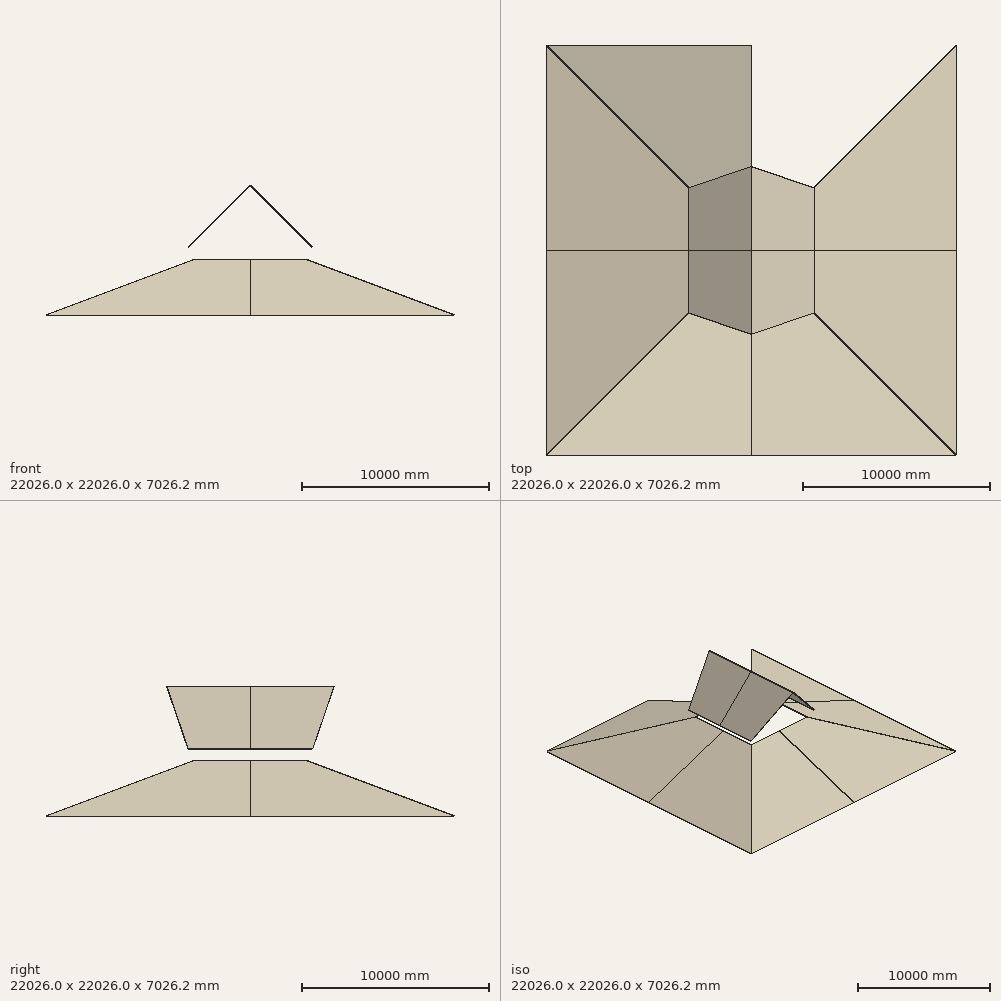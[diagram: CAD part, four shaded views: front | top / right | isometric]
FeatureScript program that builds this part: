
annotation { "Feature Type Name" : "Feature", "Feature Type Description" : "" }
export const myFeature = defineFeature(function(context is Context, id is Id, definition is map)
    precondition{}
    {
        {
            var Q0;
            Q0=qCreatedBy(makeId("Top.planeOp"),FACE);
            var sketch = newSketch(context, id + "F0", { "sketchPlane" : qUnion([Q0])});
            skLineSegment(sketch, "E0", {"start": v(0, 0) * mm, "end": v(0, -6000) * mm, "construction": true});
            skLineSegment(sketch, "E1", {"start": v(0, -6000) * mm, "end": v(6000, -6000) * mm, "construction": true});
            skLineSegment(sketch, "E2", {"start": v(6000, -6000) * mm, "end": v(6000, 0) * mm, "construction": true});
            skLineSegment(sketch, "E3", {"start": v(6000, 0) * mm, "end": v(10000, 0) * mm, "construction": true});
            skLineSegment(sketch, "E4", {"start": v(10000, 0) * mm, "end": v(10000, -10000) * mm, "construction": true});
            skLineSegment(sketch, "E5", {"start": v(10000, -10000) * mm, "end": v(-4000, -10000) * mm, "construction": true});
            skLineSegment(sketch, "E6", {"start": v(-4000, -10000) * mm, "end": v(-4000, 0) * mm, "construction": true});
            skLineSegment(sketch, "E7", {"start": v(-4000, 0) * mm, "end": v(0, 0) * mm, "construction": true});
            skLineSegment(sketch, "E8", {"start": v(3000, -6000) * mm, "end": v(3000, -8482.28) * mm, "construction": true});
            skLineSegment(sketch, "E9", {"start": v(0, -6000) * mm, "end": v(0, -10000) * mm, "construction": true});
            skLineSegment(sketch, "E10", {"start": v(-1000, 0) * mm, "end": v(-1000, -7000) * mm, "construction": true});
            skLineSegment(sketch, "E11", {"start": v(-1000, -7000) * mm, "end": v(7000, -7000) * mm, "construction": true});
            skLineSegment(sketch, "E12", {"start": v(7000, -7000) * mm, "end": v(7000, 0) * mm, "construction": true});
            skLineSegment(sketch, "E13", {"start": v(0, -6000) * mm, "end": v(-8000, -14000) * mm, "construction": true});
            skLineSegment(sketch, "E14", {"start": v(0, -3000) * mm, "end": v(-8000, -3000) * mm, "construction": true});
            skLineSegment(sketch, "E15", {"start": v(-8000, -3000) * mm, "end": v(-8000, -14000) * mm, "construction": true});
            skLineSegment(sketch, "E16", {"start": v(-8000, -14000) * mm, "end": v(3000, -14000) * mm, "construction": true});
            skLineSegment(sketch, "E17", {"start": v(3000, -14000) * mm, "end": v(3000, -6000) * mm, "construction": true});
            skLineSegment(sketch, "E18", {"start": v(0, -3000) * mm, "end": v(3000, -3000) * mm, "construction": true});
            skLineSegment(sketch, "E19", {"start": v(3000, -3000) * mm, "end": v(3000, -6000) * mm, "construction": true});
            skLineSegment(sketch, "E20", {"start": v(0, -3000) * mm, "end": v(0, -6000) * mm});
            skLineSegment(sketch, "E21", {"start": v(0, -6000) * mm, "end": v(-4000, -10000) * mm});
            skLineSegment(sketch, "E22", {"start": v(-4000, -10000) * mm, "end": v(-4000, -3000) * mm});
            skLineSegment(sketch, "E23", {"start": v(-4000, -3000) * mm, "end": v(-4000, -3000) * mm});
            skLineSegment(sketch, "E24", {"start": v(0, -3000) * mm, "end": v(-4000, -3000) * mm});
            skSolve(sketch);
        }
        {
            var Q0;
            Q0=qCreatedBy(makeId("Right.planeOp"),FACE);
            var sketch = newSketch(context, id + "F1", { "sketchPlane" : qUnion([Q0])});
            skLineSegment(sketch, "E25", {"start": v(-6000, 0) * mm, "end": v(-6000, 3000) * mm});
            skLineSegment(sketch, "E26", {"start": v(-6000, 3000) * mm, "end": v(-14000, 0) * mm});
            skLineSegment(sketch, "E27", {"start": v(-14000, 0) * mm, "end": v(-6000, 0) * mm});
            skLineSegment(sketch, "E28", {"start": v(-10000, 0) * mm, "end": v(-10000, 1500) * mm, "construction": true});
            skSolve(sketch);
        }
        {
            var Q0;
            Q0=qCreatedBy(makeId("Front.planeOp"),FACE);
            var sketch = newSketch(context, id + "F2", { "sketchPlane" : qUnion([Q0])});
            skLineSegment(sketch, "E29", {"start": v(0, 0) * mm, "end": v(0, 3000) * mm});
            skLineSegment(sketch, "E30", {"start": v(0, 3000) * mm, "end": v(-8000, 0) * mm});
            skLineSegment(sketch, "E31", {"start": v(-8000, 0) * mm, "end": v(0, 0) * mm});
            skLineSegment(sketch, "E32", {"start": v(-4000, 0) * mm, "end": v(-4000, 1500) * mm, "construction": true});
            skSolve(sketch);
        }
        {
            var Q0;
            Q0=makeQuery(id+"F2.imprint","IMPRINT",FACE,{"disambiguationData":[TD([[makeQuery(id+"F2.imprint","IMPRINT",EDGE,{"derivedFrom":sQuery(id+"F2.wireOp",EDGE,"E29")}),1.0]])]});
            cPlane(context, id + "F3", {"entities" : qUnion([Q0]), "cplaneType" : CPlaneType.OFFSET, "offset" : 6000 * mm, "width" : 150 * mm, "height" : 150 * mm});
        }
        {
            var Q0;
            Q0=qCreatedBy(id+"F3.planeOp",FACE);
            var sketch = newSketch(context, id + "F4", { "sketchPlane" : qUnion([Q0])});
            skLineSegment(sketch, "E33", {"start": v(0, 0) * mm, "end": v(0, 3000) * mm});
            skLineSegment(sketch, "E34", {"start": v(0, 3000) * mm, "end": v(-8000, 0) * mm});
            skLineSegment(sketch, "E35", {"start": v(-8000, 0) * mm, "end": v(0, 0) * mm});
            skLineSegment(sketch, "E36", {"start": v(-4000, 0) * mm, "end": v(-4000, 1500) * mm, "construction": true});
            skLineSegment(sketch, "E37", {"start": v(0, 0) * mm, "end": v(0, -3000) * mm});
            skLineSegment(sketch, "E38", {"start": v(0, -3000) * mm, "end": v(0, -3000) * mm});
            skLineSegment(sketch, "E39", {"start": v(0, 4000) * mm, "end": v(0, 3000) * mm});
            skLineSegment(sketch, "E40", {"start": v(0, 3000) * mm, "end": v(0, 4000) * mm});
            skSolve(sketch);
        }
        {
            var Q0;
            Q0=sQuery(id+"F0.wireOp",EDGE,"E18");
            var Q1;
            Q1=sQuery(id+"F0.wireOp",VERTEX,"E18.end");
            cPlane(context, id + "F5", {"entities" : qUnion([Q0, Q1]), "cplaneType" : CPlaneType.LINE_POINT, "offset" : 25 * mm, "width" : 150 * mm, "height" : 150 * mm});
        }
        {
            var Q0;
            Q0=qCreatedBy(id+"F5.planeOp",FACE);
            var sketch = newSketch(context, id + "F6", { "sketchPlane" : qUnion([Q0])});
            skLineSegment(sketch, "E41", {"start": v(-3000, 7000) * mm, "end": v(-7500, 7000) * mm, "construction": true});
            skLineSegment(sketch, "E42", {"start": v(-7500, 7000) * mm, "end": v(-6500, 4000) * mm, "construction": true});
            skLineSegment(sketch, "E43", {"start": v(-6500, 4000) * mm, "end": v(-6500, 7000) * mm, "construction": true});
            skLineSegment(sketch, "E44", {"start": v(-3000, 0) * mm, "end": v(-3000, 7000) * mm, "construction": true});
            skLineSegment(sketch, "E45", {"start": v(-6500, 4000) * mm, "end": v(-3000, 4000) * mm, "construction": true});
            skSolve(sketch);
        }
        {
            var Q0;
            Q0=sQuery(id+"F6.wireOp",EDGE,"E41");
            cPoint(context, id + "F7", {"entities" : qUnion([Q0]), "parameter" : 0.5});
        }
        {
            var Q0;
            Q0=sQuery(id+"F6.wireOp",VERTEX,"E41.end");
            var Q1;
            Q1=sQuery(id+"F4.wireOp",VERTEX,"E39.start");
            var Q2;
            Q2 = qCreatedBy(id + "F7" ,VERTEX);
            cPlane(context, id + "F8", {"entities" : qUnion([Q0, Q1, Q2]), "cplaneType" : CPlaneType.THREE_POINT, "offset" : 25 * mm, "width" : 150 * mm, "height" : 150 * mm});
        }
        {
            var Q0;
            Q0=qCreatedBy(id+"F8.planeOp",FACE);
            var sketch = newSketch(context, id + "F9", { "sketchPlane" : qUnion([Q0])});
            skLineSegment(sketch, "E46", {"start": v(7500, 7071.07) * mm, "end": v(6353.98, 2328.43) * mm});
            skLineSegment(sketch, "E47", {"start": v(6353.98, 2328.43) * mm, "end": v(3000, 2328.43) * mm});
            skLineSegment(sketch, "E48", {"start": v(3000, 2328.43) * mm, "end": v(3000, 7071.07) * mm});
            skLineSegment(sketch, "E49", {"start": v(3000, 7071.07) * mm, "end": v(7500, 7071.07) * mm});
            skLineSegment(sketch, "E50", {"start": v(6000, 2328.43) * mm, "end": v(6000, 2828.43) * mm, "construction": true});
            skLineSegment(sketch, "E51", {"start": v(6000, 2828.43) * mm, "end": v(3000, 2828.43) * mm, "construction": true});
            skSolve(sketch);
        }
        {
            var Q0;
            Q0=sQuery(id+"F4.wireOp",VERTEX,"E34.end");
            var Q1;
            Q1=sQuery(id+"F2.wireOp",VERTEX,"E31.start");
            var Q2;
            Q2=sQuery(id+"F2.wireOp",VERTEX,"E32.end");
            cPlane(context, id + "F10", {"entities" : qUnion([Q0, Q1, Q2]), "cplaneType" : CPlaneType.THREE_POINT, "offset" : 25 * mm, "width" : 150 * mm, "height" : 150 * mm});
        }
        {
            var Q0;
            Q0=qCreatedBy(id+"F10.planeOp",FACE);
            var sketch = newSketch(context, id + "F11", { "sketchPlane" : qUnion([Q0])});
            skLineSegment(sketch, "E52", {"start": v(1053.37, -3000) * mm, "end": v(-7490.63, -3000) * mm});
            skLineSegment(sketch, "E53", {"start": v(-7490.63, -3000) * mm, "end": v(-7490.63, -14000) * mm});
            skLineSegment(sketch, "E54", {"start": v(-7490.63, -14000) * mm, "end": v(1053.37, -6000) * mm});
            skLineSegment(sketch, "E55", {"start": v(1053.37, -6000) * mm, "end": v(1053.37, -3000) * mm});
            skSolve(sketch);
        }
        {
            var Q0;
            Q0=sQuery(id+"F0.wireOp",EDGE,"E0");
            cPoint(context, id + "F12", {"entities" : qUnion([Q0]), "parameter" : 0.5});
        }
        {
            var Q0;
            Q0=sQuery(id+"F11.wireOp",VERTEX,"E52.start");
            var Q1;
            Q1=sQuery(id+"F0.wireOp",VERTEX,"E14.end");
            var Q2;
            Q2 = qCreatedBy(id + "F12" ,VERTEX);
            cPlane(context, id + "F13", {"entities" : qUnion([Q0, Q1, Q2]), "cplaneType" : CPlaneType.THREE_POINT, "offset" : 25 * mm, "width" : 150 * mm, "height" : 150 * mm});
        }
        {
            var Q0;
            Q0=makeQuery(id+"F11.imprint","IMPRINT",FACE,{"disambiguationData":[TD([[makeQuery(id+"F11.imprint","IMPRINT",EDGE,{"derivedFrom":sQuery(id+"F11.wireOp",EDGE,"E52")}),1.0]])]});
            extrude(context, id + "F14", {"entities" : qUnion([Q0]), "depth" : 37 * mm, "offsetDistance" : 25 * mm});
        }
        {
            var Q0;
            Q0=makeQuery(id+"F9.imprint","IMPRINT",FACE,{"disambiguationData":[TD([[makeQuery(id+"F9.imprint","IMPRINT",EDGE,{"derivedFrom":sQuery(id+"F9.wireOp",EDGE,"E46")}),-1.0]])]});
            extrude(context, id + "F15", {"entities" : qUnion([Q0]), "depth" : 37 * mm, "offsetDistance" : 25 * mm});
        }
        {
            var Q0;
            Q0=makeQuery(id+"F15.opExtrude","SWEPT_BODY",BODY,{"disambiguationData":[OSD([sQuery(id+"F9.wireOp",EDGE,"E46"),sQuery(id+"F9.wireOp",EDGE,"E47"),sQuery(id+"F9.wireOp",EDGE,"E48"),sQuery(id+"F9.wireOp",EDGE,"E49")])]});
            var Q1;
            Q1=qCreatedBy(id+"F5.planeOp",FACE);
            mirror(context, id + "F16", {"entities" : qUnion([Q0]), "mirrorPlane" : qUnion([Q1])});
        }
        {
            var Q0;
            Q0=sQuery(id+"F0.wireOp",EDGE,"E13");
            cPoint(context, id + "F17", {"entities" : qUnion([Q0]), "parameter" : 0.5});
        }
        {
            var Q0;
            Q0=makeQuery(id+"F14.opExtrude","CAP_VERTEX",VERTEX,{"disambiguationData":[OSD([sQuery(id+"F11.wireOp",EDGE,"E54"),sQuery(id+"F11.wireOp",EDGE,"E55")])],"isStart":true});
            var Q1;
            Q1=sQuery(id+"F0.wireOp",VERTEX,"E0.end");
            var Q2;
            Q2 = qCreatedBy(id + "F17" ,VERTEX);
            cPlane(context, id + "F18", {"entities" : qUnion([Q0, Q1, Q2]), "cplaneType" : CPlaneType.THREE_POINT, "offset" : 25 * mm, "width" : 150 * mm, "height" : 150 * mm});
        }
        {
            var Q0;
            Q0=makeQuery(id+"F14.opExtrude","SWEPT_BODY",BODY,{"disambiguationData":[OSD([sQuery(id+"F11.wireOp",EDGE,"E52"),sQuery(id+"F11.wireOp",EDGE,"E53"),sQuery(id+"F11.wireOp",EDGE,"E54"),sQuery(id+"F11.wireOp",EDGE,"E55")])]});
            var Q1;
            Q1=qCreatedBy(id+"F18.planeOp",FACE);
            mirror(context, id + "F19", {"entities" : qUnion([Q0]), "mirrorPlane" : qUnion([Q1])});
        }
        {
            var Q0;
            Q0=makeQuery(id+"F14.opExtrude","SWEPT_BODY",BODY,{"disambiguationData":[OSD([sQuery(id+"F11.wireOp",EDGE,"E52"),sQuery(id+"F11.wireOp",EDGE,"E53"),sQuery(id+"F11.wireOp",EDGE,"E54"),sQuery(id+"F11.wireOp",EDGE,"E55")])]});
            var Q1;
            Q1=makeQuery(id+"F19.opPattern","COPY",BODY,{"derivedFrom":makeQuery(id+"F14.opExtrude","SWEPT_BODY",BODY,{"disambiguationData":[OSD([sQuery(id+"F11.wireOp",EDGE,"E52"),sQuery(id+"F11.wireOp",EDGE,"E53"),sQuery(id+"F11.wireOp",EDGE,"E54"),sQuery(id+"F11.wireOp",EDGE,"E55")])]}),"instanceName":"1"});
            var Q2;
            Q2=qCreatedBy(id+"F5.planeOp",FACE);
            mirror(context, id + "F20", {"operationType" : NewBodyOperationType.ADD, "entities" : qUnion([Q0, Q1]), "mirrorPlane" : qUnion([Q2])});
        }
        {
            var Q0;
            Q0=makeQuery(id+"F15.opExtrude","SWEPT_BODY",BODY,{"disambiguationData":[OSD([sQuery(id+"F9.wireOp",EDGE,"E46"),sQuery(id+"F9.wireOp",EDGE,"E47"),sQuery(id+"F9.wireOp",EDGE,"E48"),sQuery(id+"F9.wireOp",EDGE,"E49")])]});
            var Q1;
            Q1=makeQuery(id+"F16.opPattern","COPY",BODY,{"derivedFrom":makeQuery(id+"F15.opExtrude","SWEPT_BODY",BODY,{"disambiguationData":[OSD([sQuery(id+"F9.wireOp",EDGE,"E46"),sQuery(id+"F9.wireOp",EDGE,"E47"),sQuery(id+"F9.wireOp",EDGE,"E48"),sQuery(id+"F9.wireOp",EDGE,"E49")])]}),"instanceName":"1"});
            var Q2;
            Q2=qCreatedBy(id+"F13.planeOp",FACE);
            mirror(context, id + "F21", {"entities" : qUnion([Q0, Q1]), "mirrorPlane" : qUnion([Q2])});
        }
        {
            var Q0;
            Q0=makeQuery(id+"F14.opExtrude","SWEPT_BODY",BODY,{"disambiguationData":[OSD([sQuery(id+"F11.wireOp",EDGE,"E52"),sQuery(id+"F11.wireOp",EDGE,"E53"),sQuery(id+"F11.wireOp",EDGE,"E54"),sQuery(id+"F11.wireOp",EDGE,"E55")])]});
            var Q1;
            Q1=makeQuery(id+"F19.opPattern","COPY",BODY,{"derivedFrom":makeQuery(id+"F14.opExtrude","SWEPT_BODY",BODY,{"disambiguationData":[OSD([sQuery(id+"F11.wireOp",EDGE,"E52"),sQuery(id+"F11.wireOp",EDGE,"E53"),sQuery(id+"F11.wireOp",EDGE,"E54"),sQuery(id+"F11.wireOp",EDGE,"E55")])]}),"instanceName":"1"});
            var Q2;
            Q2=makeQuery(id+"F20.opPattern","COPY",BODY,{"derivedFrom":makeQuery(id+"F14.opExtrude","SWEPT_BODY",BODY,{"disambiguationData":[OSD([sQuery(id+"F11.wireOp",EDGE,"E52"),sQuery(id+"F11.wireOp",EDGE,"E53"),sQuery(id+"F11.wireOp",EDGE,"E54"),sQuery(id+"F11.wireOp",EDGE,"E55")])]}),"instanceName":"1"});
            var Q3;
            Q3=qCreatedBy(id+"F13.planeOp",FACE);
            mirror(context, id + "F22", {"entities" : qUnion([Q0, Q1, Q2]), "mirrorPlane" : qUnion([Q3])});
        }
    });
